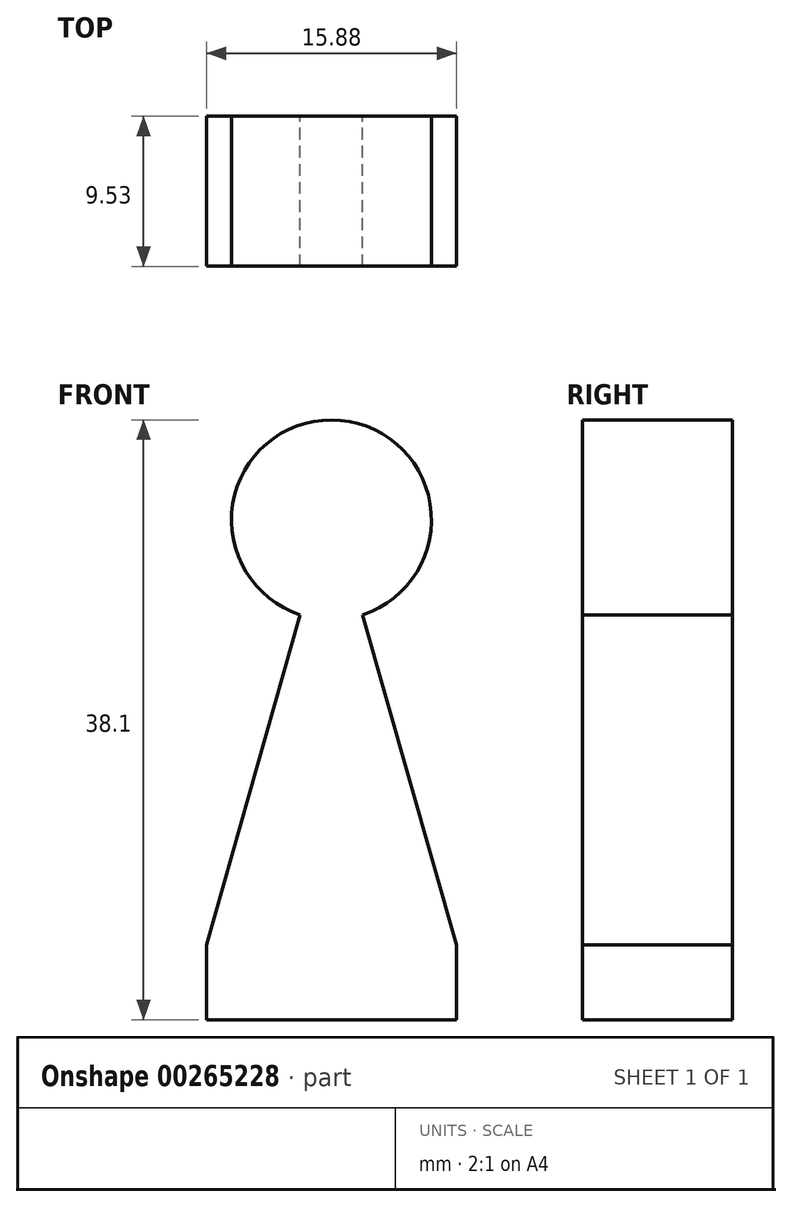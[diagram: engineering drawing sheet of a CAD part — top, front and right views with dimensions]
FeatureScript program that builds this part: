
annotation { "Feature Type Name" : "Feature", "Feature Type Description" : "" }
export const myFeature = defineFeature(function(context is Context, id is Id, definition is map)
    precondition{}
    {
        {
            var Q0;
            Q0=qCreatedBy(makeId("Front.planeOp"),FACE);
            var sketch = newSketch(context, id + "F0", { "sketchPlane" : qUnion([Q0])});
            skLineSegment(sketch, "E0", {"start": v(-7.94, -6.5) * mm, "end": v(7.94, -6.5) * mm});
            skLineSegment(sketch, "E1", {"start": v(7.94, -6.5) * mm, "end": v(7.94, -1.73) * mm});
            skLineSegment(sketch, "E2", {"start": v(7.94, -1.73) * mm, "end": v(1.98, 19.22) * mm});
            skPoint(sketch, "E3", {"position": v(0, -6.5) * mm});
            skArc(sketch, "E4", {"start": v(1.98, 19.22) * mm, "mid": v(0, 31.6) * mm, "end": v(-1.98, 19.22) * mm});
            skLineSegment(sketch, "E5.MirrorCS", {"start": v(-7.94, -1.73) * mm, "end": v(-1.98, 19.22) * mm});
            skLineSegment(sketch, "E6.MirrorCS", {"start": v(-7.94, -6.5) * mm, "end": v(-7.94, -1.73) * mm});
            skSolve(sketch);
        }
        {
            var Q0;
            Q0 = qSketchRegion(id + "F0", true);
            extrude(context, id + "F1", {"entities" : qUnion([Q0]), "depth" : 9.52 * mm});
        }
    });
